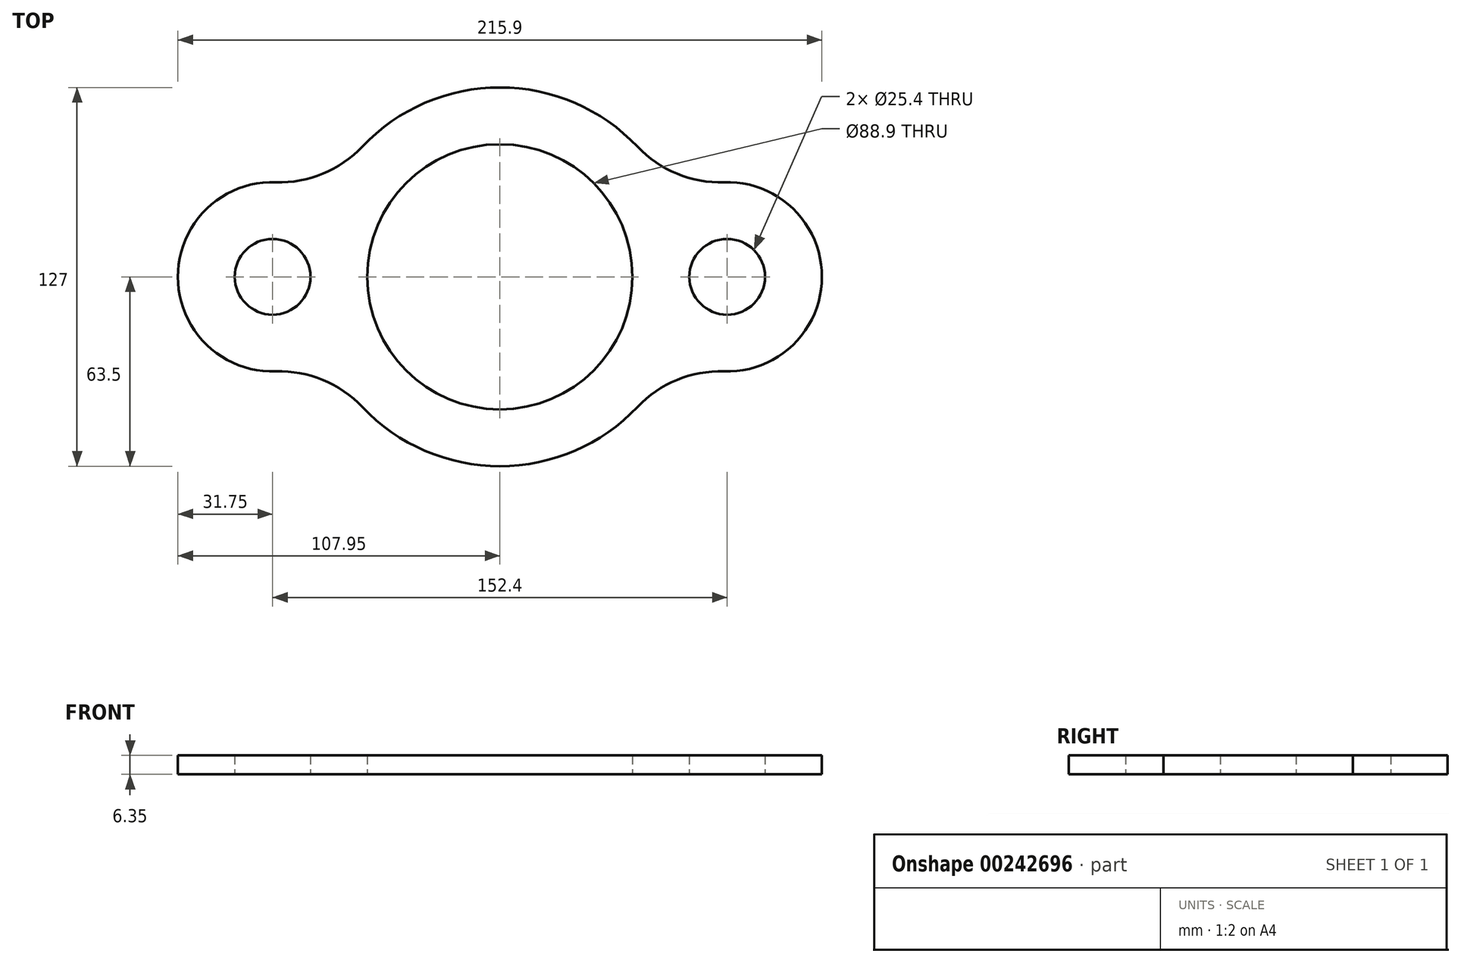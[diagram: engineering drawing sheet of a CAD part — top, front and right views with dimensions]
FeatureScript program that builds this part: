
annotation { "Feature Type Name" : "Feature", "Feature Type Description" : "" }
export const myFeature = defineFeature(function(context is Context, id is Id, definition is map)
    precondition{}
    {
        {
            var Q0;
            Q0=qCreatedBy(makeId("Top.planeOp"),FACE);
            var sketch = newSketch(context, id + "F0", { "sketchPlane" : qUnion([Q0])});
            skCircle(sketch, "E0", {"center": v(0, 0) * mm, "radius": 44.45 * mm});
            skArc(sketch, "E1", {"start": v(-46.14, -43.63) * mm, "mid": v(0, -63.5) * mm, "end": v(46.14, -43.63) * mm});
            skArc(sketch, "E2", {"start": v(-75.12, 31.73) * mm, "mid": v(-107.95, 0) * mm, "end": v(-75.12, -31.73) * mm});
            skCircle(sketch, "E3", {"center": v(-76.2, 0) * mm, "radius": 12.7 * mm});
            skCircle(sketch, "E4", {"center": v(76.2, 0) * mm, "radius": 12.7 * mm});
            skArc(sketch, "E5", {"start": v(75.12, -31.73) * mm, "mid": v(107.95, 0) * mm, "end": v(75.12, 31.73) * mm});
            skArc(sketch, "E6.trimOffspring", {"start": v(46.14, 43.63) * mm, "mid": v(0, 63.5) * mm, "end": v(-46.14, 43.63) * mm});
            skPoint(sketch, "E7.visualSharp", {"position": v(-57.94, 25.98) * mm});
            skArc(sketch, "E7.filletArc", {"start": v(-75.12, 31.73) * mm, "mid": v(-59.35, 34.56) * mm, "end": v(-46.14, 43.63) * mm});
            skPoint(sketch, "E8.visualSharp", {"position": v(57.94, 25.98) * mm});
            skArc(sketch, "E8.filletArc", {"start": v(46.14, 43.63) * mm, "mid": v(59.35, 34.56) * mm, "end": v(75.12, 31.73) * mm});
            skPoint(sketch, "E9.visualSharp", {"position": v(57.94, -25.98) * mm});
            skArc(sketch, "E9.filletArc", {"start": v(75.12, -31.73) * mm, "mid": v(59.35, -34.56) * mm, "end": v(46.14, -43.63) * mm});
            skPoint(sketch, "E10.visualSharp", {"position": v(-57.94, -25.98) * mm});
            skArc(sketch, "E10.filletArc", {"start": v(-46.14, -43.63) * mm, "mid": v(-59.35, -34.56) * mm, "end": v(-75.12, -31.73) * mm});
            skSolve(sketch);
        }
        {
            var Q0;
            Q0 = qSketchRegion(id + "F0", true);
            extrude(context, id + "F1", {"entities" : qUnion([Q0]), "depth" : 6.35 * mm});
        }
    });
